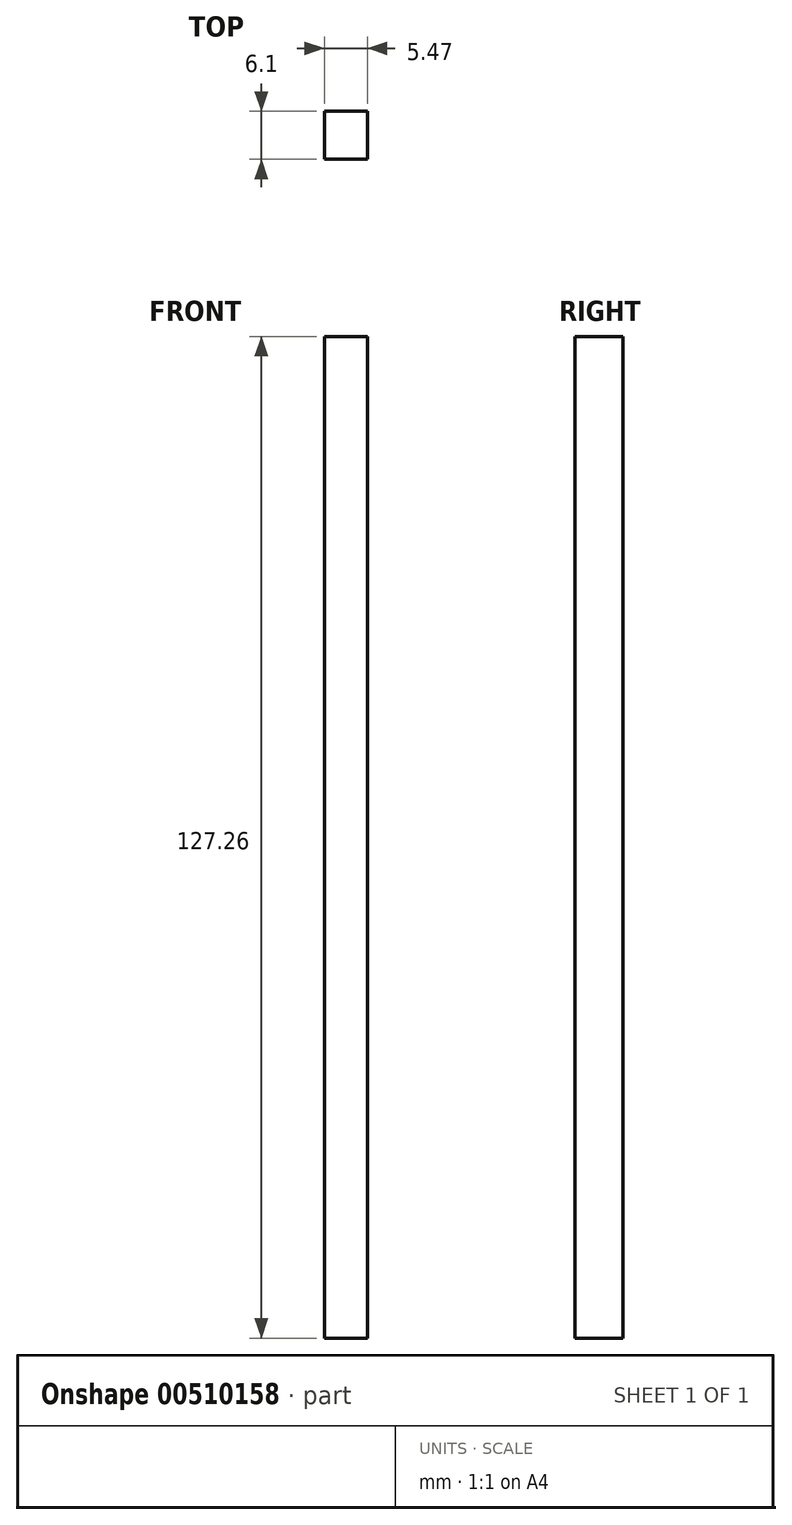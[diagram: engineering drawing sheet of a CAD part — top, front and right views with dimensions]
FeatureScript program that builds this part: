
annotation { "Feature Type Name" : "Feature", "Feature Type Description" : "" }
export const myFeature = defineFeature(function(context is Context, id is Id, definition is map)
    precondition{}
    {
        {
            var Q0;
            Q0=qCreatedBy(makeId("Front.planeOp"),FACE);
            var sketch = newSketch(context, id + "F0", { "sketchPlane" : qUnion([Q0])});
            skLineSegment(sketch, "E0", {"start": v(-30.25, -31.25) * mm, "end": v(-24.78, -31.25) * mm});
            skLineSegment(sketch, "E1", {"start": v(-24.78, -31.25) * mm, "end": v(-24.78, 96) * mm});
            skLineSegment(sketch, "E2", {"start": v(-24.78, 96) * mm, "end": v(-30.25, 96) * mm});
            skLineSegment(sketch, "E3", {"start": v(-30.25, 96) * mm, "end": v(-30.25, -31.25) * mm});
            skSolve(sketch);
        }
        {
            var Q0;
            Q0=makeQuery(id+"F0.imprint","IMPRINT",FACE,{"disambiguationData":[TD([[makeQuery(id+"F0.imprint","IMPRINT",EDGE,{"derivedFrom":sQuery(id+"F0.wireOp",EDGE,"E0")}),1.0]])]});
            extrude(context, id + "F1", {"entities" : qUnion([Q0]), "depth" : 6.1 * mm, "offsetDistance" : 25.4 * mm});
        }
    });
